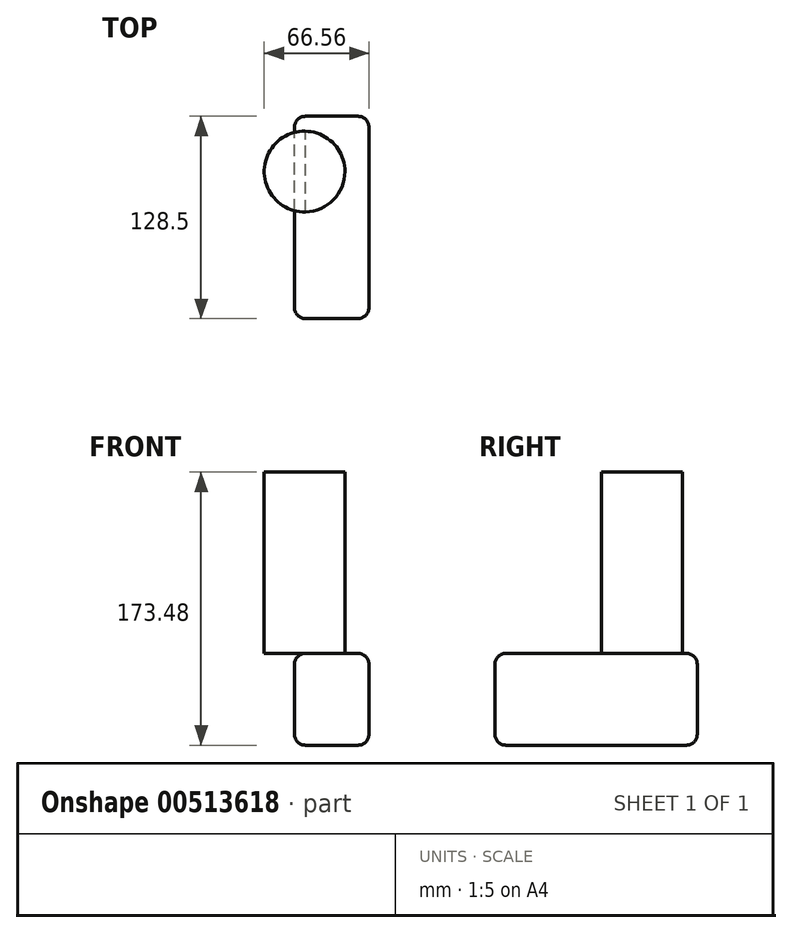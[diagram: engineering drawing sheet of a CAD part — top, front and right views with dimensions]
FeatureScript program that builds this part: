
annotation { "Feature Type Name" : "Feature", "Feature Type Description" : "" }
export const myFeature = defineFeature(function(context is Context, id is Id, definition is map)
    precondition{}
    {
        {
            var Q0;
            Q0=qCreatedBy(makeId("Front.planeOp"),FACE);
            var sketch = newSketch(context, id + "F0", { "sketchPlane" : qUnion([Q0])});
            skLineSegment(sketch, "E0.bottom", {"start": v(0, 0) * mm, "end": v(47.34, 0) * mm});
            skLineSegment(sketch, "E0.top", {"start": v(0, 58.37) * mm, "end": v(47.34, 58.37) * mm});
            skLineSegment(sketch, "E0.left", {"start": v(0, 0) * mm, "end": v(0, 58.37) * mm});
            skLineSegment(sketch, "E0.right", {"start": v(47.34, 0) * mm, "end": v(47.34, 58.37) * mm});
            skSolve(sketch);
        }
        {
            var Q0;
            Q0=makeQuery(id+"F0.imprint","IMPRINT",FACE,{"disambiguationData":[TD([[makeQuery(id+"F0.imprint","IMPRINT",EDGE,{"derivedFrom":sQuery(id+"F0.wireOp",EDGE,"E0.bottom")}),1.0]])]});
            extrude(context, id + "F1", {"entities" : qUnion([Q0]), "depth" : 128.5 * mm, "offsetDistance" : 25.4 * mm});
        }
        {
            var Q0;
            Q0=makeQuery(id+"F1.opExtrude","CAP_EDGE",EDGE,{"disambiguationData":[OSD([sQuery(id+"F0.wireOp",EDGE,"E0.top")])],"isStart":false});
            var Q1;
            Q1=makeQuery(id+"F1.opExtrude","SWEPT_EDGE",EDGE,{"disambiguationData":[OSD([sQuery(id+"F0.wireOp",EDGE,"E0.top"),sQuery(id+"F0.wireOp",EDGE,"E0.right")])]});
            var Q2;
            Q2=makeQuery(id+"F1.opExtrude","SWEPT_EDGE",EDGE,{"disambiguationData":[OSD([sQuery(id+"F0.wireOp",EDGE,"E0.top"),sQuery(id+"F0.wireOp",EDGE,"E0.left")])]});
            var Q3;
            Q3=makeQuery(id+"F1.opExtrude","CAP_EDGE",EDGE,{"disambiguationData":[OSD([sQuery(id+"F0.wireOp",EDGE,"E0.top")])],"isStart":true});
            var Q4;
            Q4=makeQuery(id+"F1.opExtrude","CAP_EDGE",EDGE,{"disambiguationData":[OSD([sQuery(id+"F0.wireOp",EDGE,"E0.right")])],"isStart":false});
            var Q5;
            Q5=makeQuery(id+"F1.opExtrude","CAP_EDGE",EDGE,{"disambiguationData":[OSD([sQuery(id+"F0.wireOp",EDGE,"E0.left")])],"isStart":false});
            var Q6;
            Q6=makeQuery(id+"F1.opExtrude","CAP_EDGE",EDGE,{"disambiguationData":[OSD([sQuery(id+"F0.wireOp",EDGE,"E0.bottom")])],"isStart":false});
            var Q7;
            Q7=makeQuery(id+"F1.opExtrude","SWEPT_EDGE",EDGE,{"disambiguationData":[OSD([sQuery(id+"F0.wireOp",EDGE,"E0.bottom"),sQuery(id+"F0.wireOp",EDGE,"E0.right")])]});
            var Q8;
            Q8=makeQuery(id+"F1.opExtrude","CAP_EDGE",EDGE,{"disambiguationData":[OSD([sQuery(id+"F0.wireOp",EDGE,"E0.right")])],"isStart":true});
            var Q9;
            Q9=makeQuery(id+"F1.opExtrude","CAP_EDGE",EDGE,{"disambiguationData":[OSD([sQuery(id+"F0.wireOp",EDGE,"E0.left")])],"isStart":true});
            var Q10;
            Q10=makeQuery(id+"F1.opExtrude","CAP_EDGE",EDGE,{"disambiguationData":[OSD([sQuery(id+"F0.wireOp",EDGE,"E0.bottom")])],"isStart":true});
            var Q11;
            Q11=makeQuery(id+"F1.opExtrude","SWEPT_FACE",FACE,{"disambiguationData":[OSD([sQuery(id+"F0.wireOp",EDGE,"E0.bottom")])]});
            fillet(context, id + "F2", {"entities" : qUnion([Q0, Q1, Q2, Q3, Q4, Q5, Q6, Q7, Q8, Q9, Q10, Q11]), "radius" : 6.97 * mm, "tangentPropagation" : true, "allowEdgeOverflow" : false});
        }
        {
            var Q0;
            Q0=makeQuery(id+"F1.opExtrude","SWEPT_FACE",FACE,{"disambiguationData":[OSD([sQuery(id+"F0.wireOp",EDGE,"E0.top")])]});
            var sketch = newSketch(context, id + "F3", { "sketchPlane" : qUnion([Q0])});
            skCircle(sketch, "E1", {"center": v(6.42, -35.1) * mm, "radius": 25.64 * mm});
            skSolve(sketch);
        }
        {
            var Q0;
            {var subQ0=sQuery(id+"F3.wireOp",EDGE,"E1");var subQ1=sQuery(id+"F0.wireOp",EDGE,"E0.top");var subQ2=makeQuery(id+"F2.opFillet","BLEND_EDGE",EDGE,{"blendedFrom":[makeQuery(id+"F1.opExtrude","SWEPT_EDGE",EDGE,{"disambiguationData":[OSD([subQ1,sQuery(id+"F0.wireOp",EDGE,"E0.left")])]}),makeQuery(id+"F1.opExtrude","SWEPT_FACE",FACE,{"disambiguationData":[OSD([subQ1])]})],"blendedInto":[makeQuery(id+"F1.opExtrude","SWEPT_FACE",FACE,{"disambiguationData":[OSD([subQ1])]})]});var subQ3=makeQuery(id+"F3.imprint","INTERSECT",VERTEX,{"disambiguationData":[OD(0.0)],"derivedFrom":[subQ2,subQ0]});Q0=makeQuery(id+"F3.imprint","IMPRINT",FACE,{"disambiguationData":[TD([[makeQuery(id+"F3.imprint","IMPRINT",EDGE,{"disambiguationData":[TD([[subQ3,-1.0]])],"derivedFrom":subQ0}),1.0]])]});}
            var Q1;
            {var subQ0=sQuery(id+"F3.wireOp",EDGE,"E1");var subQ1=sQuery(id+"F0.wireOp",EDGE,"E0.top");var subQ2=makeQuery(id+"F2.opFillet","BLEND_EDGE",EDGE,{"blendedFrom":[makeQuery(id+"F1.opExtrude","SWEPT_EDGE",EDGE,{"disambiguationData":[OSD([subQ1,sQuery(id+"F0.wireOp",EDGE,"E0.left")])]}),makeQuery(id+"F1.opExtrude","SWEPT_FACE",FACE,{"disambiguationData":[OSD([subQ1])]})],"blendedInto":[makeQuery(id+"F1.opExtrude","SWEPT_FACE",FACE,{"disambiguationData":[OSD([subQ1])]})]});var subQ3=makeQuery(id+"F3.imprint","INTERSECT",VERTEX,{"disambiguationData":[OD(0.0)],"derivedFrom":[subQ2,subQ0]});Q1=makeQuery(id+"F3.imprint","IMPRINT",FACE,{"disambiguationData":[TD([[makeQuery(id+"F3.imprint","IMPRINT",EDGE,{"disambiguationData":[TD([[subQ3,1.0]])],"derivedFrom":subQ0}),1.0]])]});}
            extrude(context, id + "F4", {"entities" : qUnion([Q0, Q1]), "operationType" : NewBodyOperationType.ADD, "depth" : 115.11 * mm, "offsetDistance" : 25.4 * mm});
        }
    });
